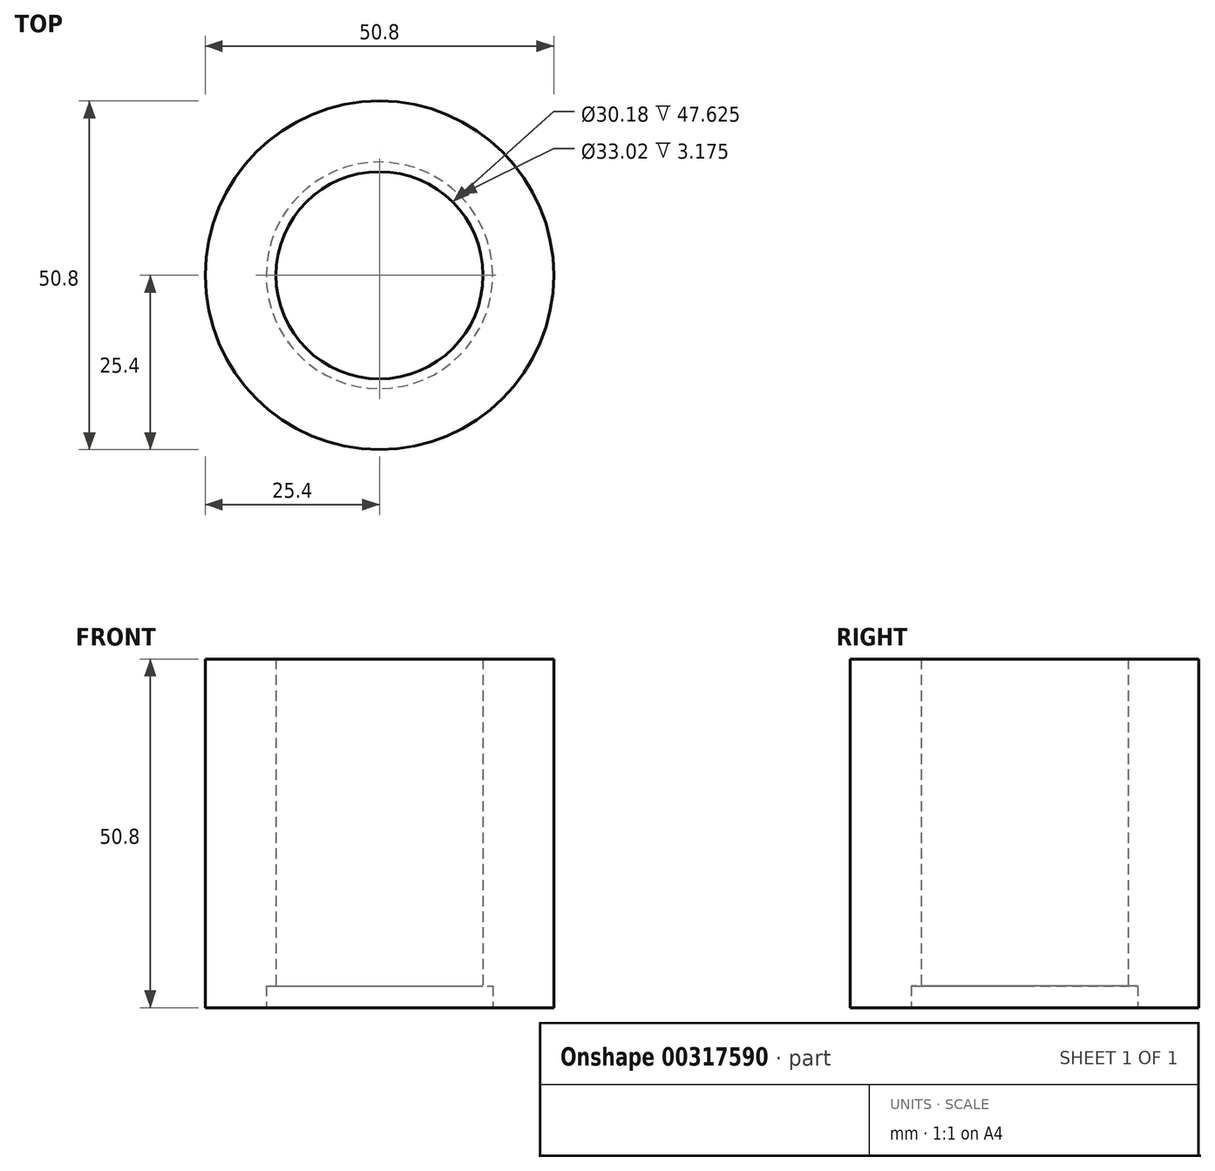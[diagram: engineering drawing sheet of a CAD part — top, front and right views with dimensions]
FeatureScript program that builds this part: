
annotation { "Feature Type Name" : "Feature", "Feature Type Description" : "" }
export const myFeature = defineFeature(function(context is Context, id is Id, definition is map)
    precondition{}
    {
        {
            var Q0;
            Q0=qCreatedBy(makeId("Top.planeOp"),FACE);
            var sketch = newSketch(context, id + "F0", { "sketchPlane" : qUnion([Q0])});
            skCircle(sketch, "E0", {"center": v(0, 0) * mm, "radius": 25.4 * mm});
            skSolve(sketch);
        }
        {
            var Q0;
            Q0=makeQuery(id+"F0.imprint","IMPRINT",FACE,{"disambiguationData":[TD([[makeQuery(id+"F0.imprint","IMPRINT",EDGE,{"derivedFrom":sQuery(id+"F0.wireOp",EDGE,"E0")}),1.0]])]});
            extrude(context, id + "F1", {"entities" : qUnion([Q0]), "depth" : 50.8 * mm});
        }
        {
            var Q0;
            Q0=makeQuery(id+"F1.opExtrude","CAP_FACE",FACE,{"disambiguationData":[OSD([sQuery(id+"F0.wireOp",EDGE,"E0")])],"isStart":true});
            var sketch = newSketch(context, id + "F2", { "sketchPlane" : qUnion([Q0])});
            skCircle(sketch, "E1", {"center": v(0, 0) * mm, "radius": 15.08 * mm});
            skSolve(sketch);
        }
        {
            var Q0;
            Q0=sQuery(id+"F2.wireOp",VERTEX,"E1.center");
            var Q1;
            Q1=makeQuery(id+"F1.opExtrude","SWEPT_BODY",BODY,{"disambiguationData":[OSD([sQuery(id+"F0.wireOp",EDGE,"E0")])]});
            hole(context, id + "F3", {"style" : HoleStyle.C_BORE, "endStyle" : HoleEndStyle.THROUGH, "holeDiameter" : 30.18 * mm, "cBoreDiameter" : 33.02 * mm, "cBoreDepth" : 3.17 * mm, "isTappedThrough" : true, "tappedDepth" : 12.7 * mm, "tapClearance" : 3, "locations" : qUnion([Q0]), "scope" : qUnion([Q1])});
        }
    });
